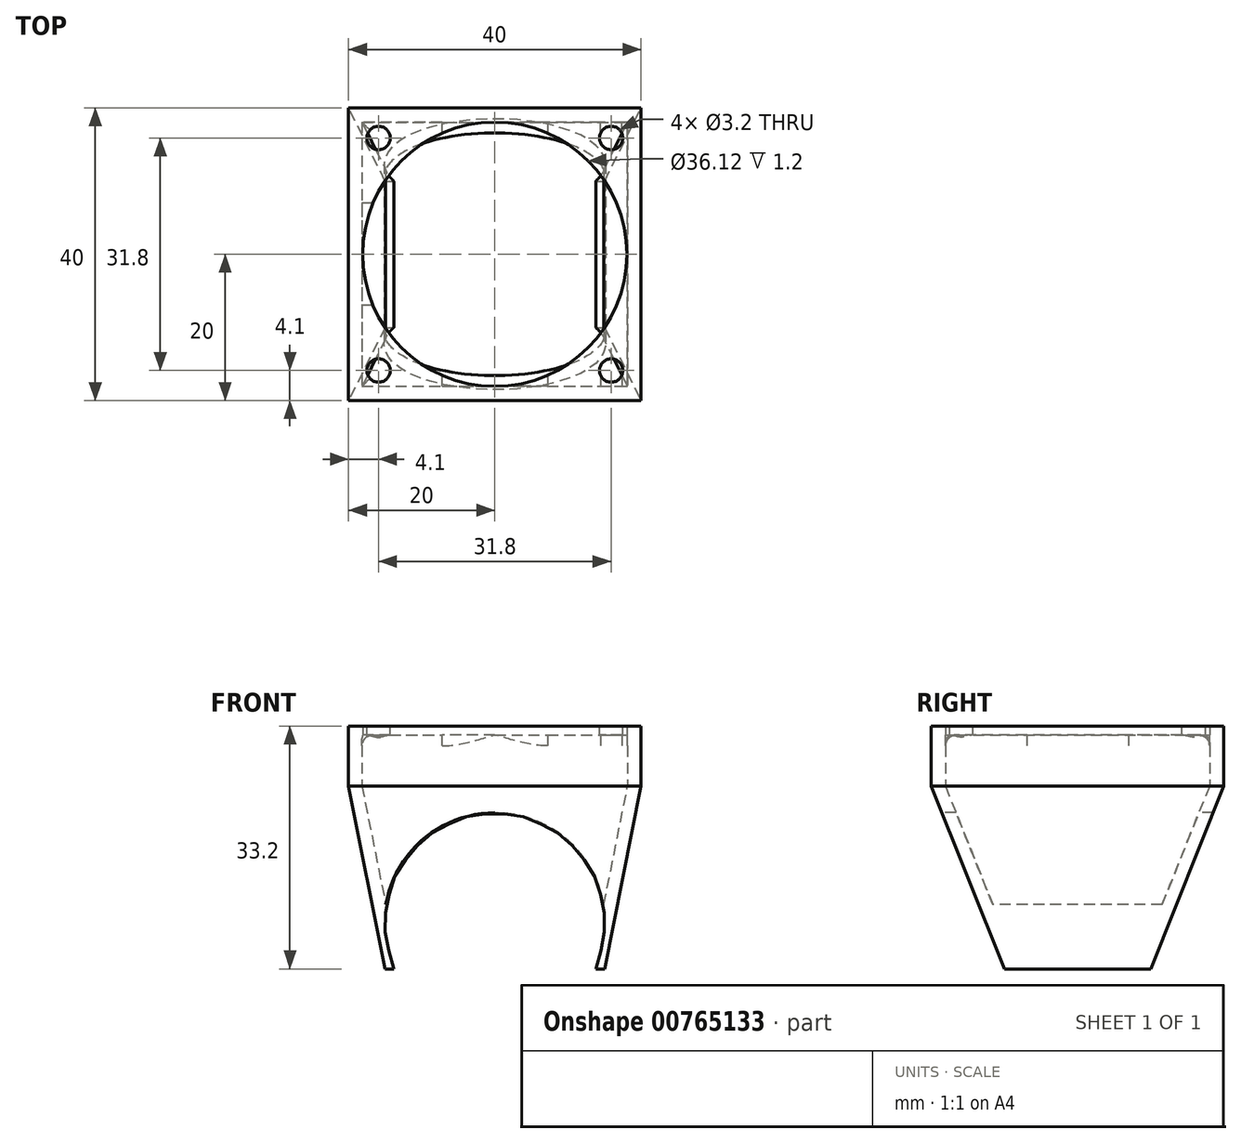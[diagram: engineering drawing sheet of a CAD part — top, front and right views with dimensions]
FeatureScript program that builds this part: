
annotation { "Feature Type Name" : "Feature", "Feature Type Description" : "" }
export const myFeature = defineFeature(function(context is Context, id is Id, definition is map)
    precondition{}
    {
        {
            var Q0;
            Q0=qCreatedBy(makeId("Top.planeOp"),FACE);
            var sketch = newSketch(context, id + "F0", { "sketchPlane" : qUnion([Q0])});
            skLineSegment(sketch, "E0.bottom", {"start": v(-15, 10) * mm, "end": v(15, 10) * mm});
            skLineSegment(sketch, "E0.top", {"start": v(-15, -10) * mm, "end": v(15, -10) * mm});
            skLineSegment(sketch, "E0.left", {"start": v(-15, 10) * mm, "end": v(-15, -10) * mm});
            skLineSegment(sketch, "E0.right", {"start": v(15, 10) * mm, "end": v(15, -10) * mm});
            skPoint(sketch, "E0.middle", {"position": v(0, 0) * mm});
            skSolve(sketch);
        }
        {
            var Q0;
            Q0=makeQuery(id+"F0.imprint","IMPRINT",FACE,{"disambiguationData":[TD([[makeQuery(id+"F0.imprint","IMPRINT",EDGE,{"derivedFrom":sQuery(id+"F0.wireOp",EDGE,"E0.bottom")}),-1.0]])]});
            cPlane(context, id + "F1", {"entities" : qUnion([Q0]), "cplaneType" : CPlaneType.OFFSET, "offset" : 25 * mm, "width" : 150 * mm, "height" : 150 * mm});
        }
        {
            var Q0;
            Q0=qCreatedBy(id+"F1.planeOp",FACE);
            var sketch = newSketch(context, id + "F2", { "sketchPlane" : qUnion([Q0])});
            skLineSegment(sketch, "E1.bottom", {"start": v(-20, 20) * mm, "end": v(20, 20) * mm});
            skLineSegment(sketch, "E1.top", {"start": v(-20, -20) * mm, "end": v(20, -20) * mm});
            skLineSegment(sketch, "E1.left", {"start": v(-20, 20) * mm, "end": v(-20, -20) * mm});
            skLineSegment(sketch, "E1.right", {"start": v(20, 20) * mm, "end": v(20, -20) * mm});
            skPoint(sketch, "E1.middle", {"position": v(0, 0) * mm});
            skSolve(sketch);
        }
        {
            var Q0;
            Q0=makeQuery(id+"F0.imprint","IMPRINT",FACE,{"disambiguationData":[TD([[makeQuery(id+"F0.imprint","IMPRINT",EDGE,{"derivedFrom":sQuery(id+"F0.wireOp",EDGE,"E0.bottom")}),-1.0]])]});
            var Q1;
            Q1=makeQuery(id+"F2.imprint","IMPRINT",FACE,{"disambiguationData":[TD([[makeQuery(id+"F2.imprint","IMPRINT",EDGE,{"derivedFrom":sQuery(id+"F2.wireOp",EDGE,"E1.bottom")}),-1.0]])]});
            loft(context, id + "F3", {"sheetProfilesArray" : [{ "sheetProfileEntities" : qUnion([Q0]) }, { "sheetProfileEntities" : qUnion([Q1]) }]});
        }
        {
            var Q0;
            Q0=makeQuery(id+"F3.opLoft","CAP_FACE",FACE,{"disambiguationData":[OSD([makeQuery(id+"F2.imprint","IMPRINT",FACE,{"disambiguationData":[TD([[makeQuery(id+"F2.imprint","IMPRINT",EDGE,{"derivedFrom":sQuery(id+"F2.wireOp",EDGE,"E1.bottom")}),-1.0]])]})])],"isStart":true});
            var Q1;
            Q1=makeQuery(id+"F3.opLoft","CAP_FACE",FACE,{"disambiguationData":[OSD([makeQuery(id+"F0.imprint","IMPRINT",FACE,{"disambiguationData":[TD([[makeQuery(id+"F0.imprint","IMPRINT",EDGE,{"derivedFrom":sQuery(id+"F0.wireOp",EDGE,"E0.bottom")}),-1.0]])]})])],"isStart":true});
            shell(context, id + "F4", {"entities" : qUnion([Q0, Q1]), "thickness" : 1.8 * mm});
        }
        {
            var Q0;
            Q0=qCreatedBy(makeId("Front.planeOp"),FACE);
            var sketch = newSketch(context, id + "F5", { "sketchPlane" : qUnion([Q0])});
            skPoint(sketch, "E2.0", {"position": v(-15, 0) * mm});
            skPoint(sketch, "E3.0", {"position": v(15, 0) * mm});
            skArc(sketch, "E4", {"start": v(13.8, 0) * mm, "mid": v(0, 21.36) * mm, "end": v(-13.8, 0) * mm});
            skLineSegment(sketch, "E5", {"start": v(-13.8, 0) * mm, "end": v(13.8, 0) * mm});
            skSolve(sketch);
        }
        {
            var Q0;
            Q0 = qSketchRegion(id + "F5", true);
            extrude(context, id + "F6", {"entities" : qUnion([Q0]), "operationType" : NewBodyOperationType.REMOVE, "oppositeDirection" : true, "depth" : 25 * mm, "offsetDistance" : 25 * mm, "hasSecondDirection" : true, "secondDirectionOppositeDirection" : false, "secondDirectionDepth" : 25 * mm});
        }
        {
            var Q0;
            Q0=makeQuery(id+"F3.opLoft","MID_CAP_EDGE",EDGE,{"disambiguationData":[OSD([sQuery(id+"F2.wireOp",EDGE,"E1.top"),sQuery(id+"F2.wireOp",EDGE,"E1.left"),sQuery(id+"F2.wireOp",EDGE,"E1.right")])],"capPos":1.0});
            cPlane(context, id + "F7", {"entities" : qUnion([Q0]), "cplaneType" : CPlaneType.LINE_ANGLE, "offset" : 0 * mm, "angle" : 90 * degree, "width" : 150 * mm, "height" : 150 * mm});
        }
        {
            var Q0;
            Q0=qCreatedBy(id+"F7.planeOp",FACE);
            var sketch = newSketch(context, id + "F8", { "sketchPlane" : qUnion([Q0])});
            skLineSegment(sketch, "E6.0", {"start": v(-20, -20) * mm, "end": v(20, -20) * mm});
            skLineSegment(sketch, "E7.0", {"start": v(-18.16, -18.06) * mm, "end": v(18.16, -18.06) * mm});
            skLineSegment(sketch, "E8.0", {"start": v(18.16, -18.06) * mm, "end": v(18.16, 18.06) * mm});
            skLineSegment(sketch, "E9.0", {"start": v(20, -20) * mm, "end": v(20, 20) * mm});
            skLineSegment(sketch, "E10.0", {"start": v(18.16, 18.06) * mm, "end": v(-18.16, 18.06) * mm});
            skLineSegment(sketch, "E11.0", {"start": v(20, 20) * mm, "end": v(-20, 20) * mm});
            skLineSegment(sketch, "E12.0", {"start": v(-20, 20) * mm, "end": v(-20, -20) * mm});
            skLineSegment(sketch, "E13.0", {"start": v(-18.16, 18.06) * mm, "end": v(-18.16, -18.06) * mm});
            skSolve(sketch);
        }
        {
            var Q0;
            Q0 = qSketchRegion(id + "F8", true);
            extrude(context, id + "F9", {"entities" : qUnion([Q0]), "operationType" : NewBodyOperationType.ADD, "depth" : 7 * mm, "offsetDistance" : 25 * mm});
        }
        {
            var Q0;
            Q0=makeQuery(id+"F9.opExtrude","CAP_EDGE",EDGE,{"disambiguationData":[OSD([sQuery(id+"F8.wireOp",EDGE,"E6.0")])],"isStart":false});
            cPlane(context, id + "F10", {"entities" : qUnion([Q0]), "cplaneType" : CPlaneType.LINE_ANGLE, "offset" : 25 * mm, "angle" : 90 * degree, "width" : 150 * mm, "height" : 150 * mm});
        }
        {
            var Q0;
            Q0=qCreatedBy(id+"F10.planeOp",FACE);
            var sketch = newSketch(context, id + "F11", { "sketchPlane" : qUnion([Q0])});
            skLineSegment(sketch, "E14.0", {"start": v(-18.16, -18.06) * mm, "end": v(18.16, -18.06) * mm});
            skLineSegment(sketch, "E15.0", {"start": v(18.16, -18.06) * mm, "end": v(18.16, 18.06) * mm});
            skLineSegment(sketch, "E16.0", {"start": v(18.16, 18.06) * mm, "end": v(-18.16, 18.06) * mm});
            skLineSegment(sketch, "E17.0", {"start": v(-18.16, 18.06) * mm, "end": v(-18.16, -18.06) * mm});
            skCircle(sketch, "E18", {"center": v(0, 0) * mm, "radius": 18.06 * mm});
            skLineSegment(sketch, "E19.0", {"start": v(-20, -20) * mm, "end": v(20, -20) * mm});
            skLineSegment(sketch, "E20.0", {"start": v(20, -20) * mm, "end": v(20, 20) * mm});
            skLineSegment(sketch, "E21.0", {"start": v(20, 20) * mm, "end": v(-20, 20) * mm});
            skLineSegment(sketch, "E22.0", {"start": v(-20, 20) * mm, "end": v(-20, -20) * mm});
            skSolve(sketch);
        }
        {
            var Q0;
            Q0 = qSketchRegion(id + "F11", true);
            var Q1;
            {var subQ0=sQuery(id+"F11.wireOp",EDGE,"E15.0");Q1=makeQuery(id+"F11.imprint","IMPRINT",FACE,{"disambiguationData":[TD([[makeQuery(id+"F11.imprint","IMPRINT",EDGE,{"derivedFrom":subQ0}),1.0]])]});}
            var Q2;
            {var subQ0=sQuery(id+"F11.wireOp",EDGE,"E17.0");Q2=makeQuery(id+"F11.imprint","IMPRINT",FACE,{"disambiguationData":[TD([[makeQuery(id+"F11.imprint","IMPRINT",EDGE,{"derivedFrom":subQ0}),1.0]])]});}
            extrude(context, id + "F12", {"entities" : qUnion([Q0, Q1, Q2]), "operationType" : NewBodyOperationType.ADD, "depth" : 1.2 * mm, "offsetDistance" : 25 * mm});
        }
        {
            var Q0;
            Q0=makeQuery(id+"F12.opExtrude","CAP_FACE",FACE,{"disambiguationData":[OSD([sQuery(id+"F11.wireOp",EDGE,"E18"),sQuery(id+"F11.wireOp",EDGE,"E19.0"),sQuery(id+"F11.wireOp",EDGE,"E20.0"),sQuery(id+"F11.wireOp",EDGE,"E21.0"),sQuery(id+"F11.wireOp",EDGE,"E22.0")])],"isStart":false});
            var sketch = newSketch(context, id + "F13", { "sketchPlane" : qUnion([Q0])});
            skCircle(sketch, "E23", {"center": v(15.9, 15.9) * mm, "radius": 1.6 * mm});
            skLineSegment(sketch, "E24", {"start": v(0, -20) * mm, "end": v(0, 20) * mm, "construction": true});
            skLineSegment(sketch, "E25", {"start": v(20, 0) * mm, "end": v(-20, 0) * mm, "construction": true});
            skCircle(sketch, "E26.MirrorC", {"center": v(-15.9, 15.9) * mm, "radius": 1.6 * mm});
            skCircle(sketch, "E27.MirrorC", {"center": v(15.9, -15.9) * mm, "radius": 1.6 * mm});
            skCircle(sketch, "E28.MirrorC", {"center": v(-15.9, -15.9) * mm, "radius": 1.6 * mm});
            skSolve(sketch);
        }
        {
            var Q0;
            Q0 = qSketchRegion(id + "F13", true);
            extrude(context, id + "F14", {"entities" : qUnion([Q0]), "operationType" : NewBodyOperationType.REMOVE, "oppositeDirection" : true, "depth" : 3 * mm, "offsetDistance" : 25 * mm});
        }
        {
            var Q0;
            {var subQ0=sQuery(id+"F8.wireOp",EDGE,"E10.0");Q0=makeQuery(id+"F12.boolean.opBoolean","SPLIT",EDGE,{"disambiguationData":[TD([makeQuery(id+"F9.opExtrude","SWEPT_FACE",FACE,{"disambiguationData":[OSD([sQuery(id+"F8.wireOp",EDGE,"E8.0")])]})])],"derivedFrom":makeQuery(id+"F9.opExtrude","CAP_EDGE",EDGE,{"disambiguationData":[OSD([subQ0])],"isStart":false})});}
            var Q1;
            Q1=makeQuery(id+"F9.opExtrude","CAP_EDGE",EDGE,{"disambiguationData":[OSD([sQuery(id+"F8.wireOp",EDGE,"E8.0")])],"isStart":false});
            var Q2;
            {var subQ0=sQuery(id+"F8.wireOp",EDGE,"E7.0");Q2=makeQuery(id+"F12.boolean.opBoolean","SPLIT",EDGE,{"disambiguationData":[TD([makeQuery(id+"F9.opExtrude","SWEPT_FACE",FACE,{"disambiguationData":[OSD([sQuery(id+"F8.wireOp",EDGE,"E8.0")])]})])],"derivedFrom":makeQuery(id+"F9.opExtrude","CAP_EDGE",EDGE,{"disambiguationData":[OSD([subQ0])],"isStart":false})});}
            var Q3;
            Q3=makeQuery(id+"F9.opExtrude","CAP_EDGE",EDGE,{"disambiguationData":[OSD([sQuery(id+"F8.wireOp",EDGE,"E13.0")])],"isStart":false});
            fillet(context, id + "F15", {"entities" : qUnion([Q0, Q1, Q2, Q3]), "radius" : 1.5 * mm, "tangentPropagation" : true, "allowEdgeOverflow" : false});
        }
    });
